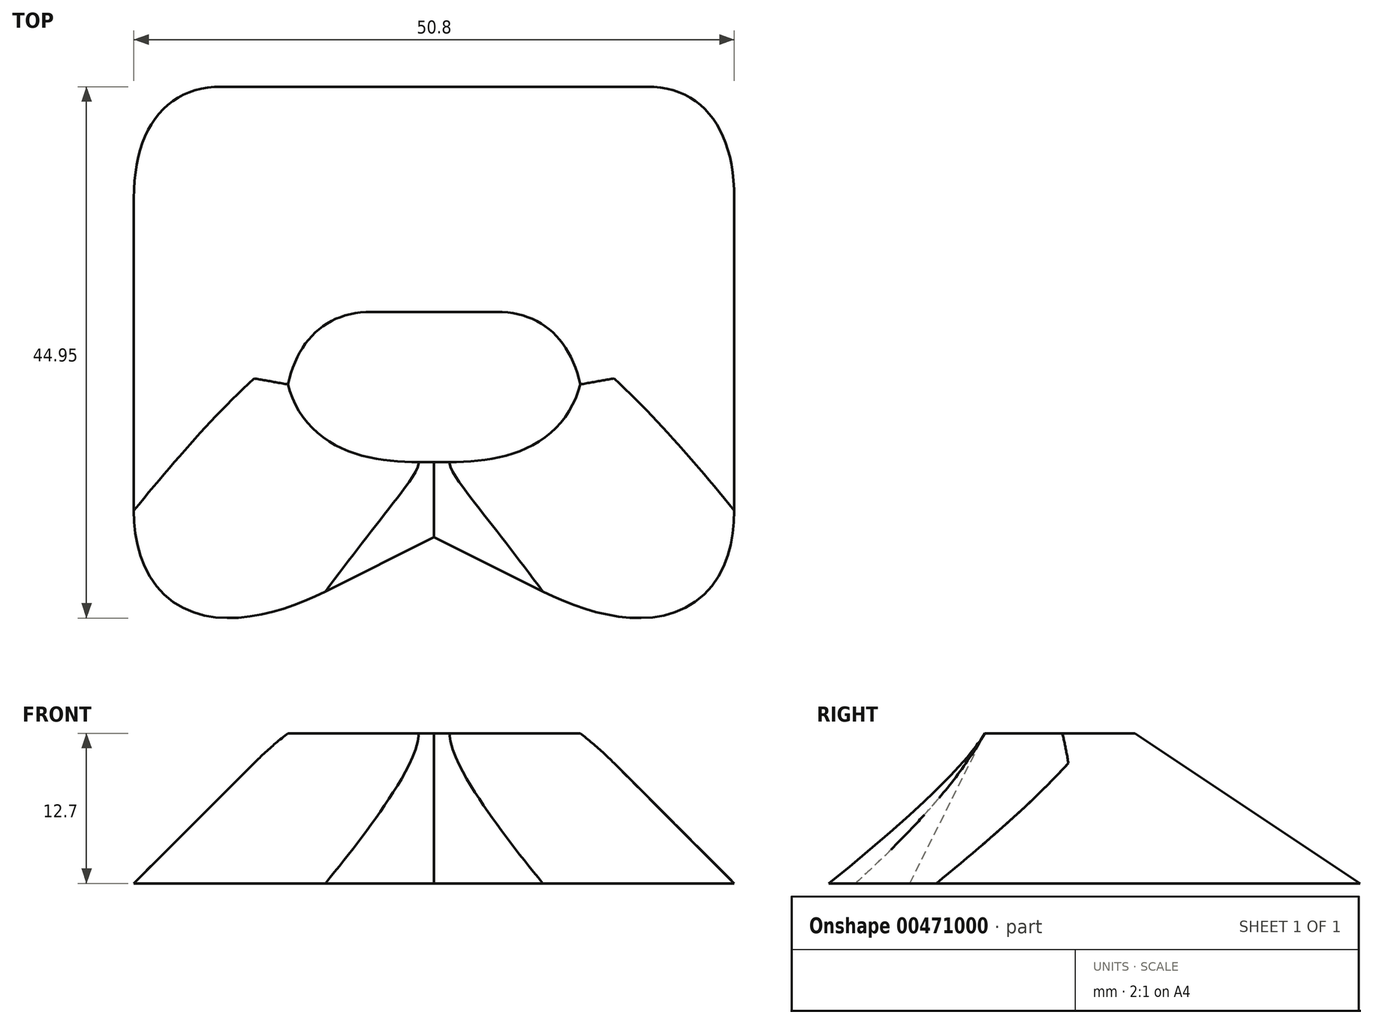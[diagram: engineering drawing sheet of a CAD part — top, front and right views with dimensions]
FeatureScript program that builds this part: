
annotation { "Feature Type Name" : "Feature", "Feature Type Description" : "" }
export const myFeature = defineFeature(function(context is Context, id is Id, definition is map)
    precondition{}
    {
        {
            var Q0;
            Q0=qCreatedBy(makeId("Top.planeOp"),FACE);
            var sketch = newSketch(context, id + "F0", { "sketchPlane" : qUnion([Q0])});
            skLineSegment(sketch, "E0", {"start": v(25.4, 25.4) * mm, "end": v(-25.4, 25.4) * mm});
            skLineSegment(sketch, "E1", {"start": v(-25.4, 25.4) * mm, "end": v(-25.4, -25.4) * mm});
            skLineSegment(sketch, "E2", {"start": v(-25.4, -25.4) * mm, "end": v(0, -12.7) * mm});
            skLineSegment(sketch, "E3", {"start": v(0, -12.7) * mm, "end": v(25.4, -25.4) * mm});
            skLineSegment(sketch, "E4", {"start": v(25.4, -25.4) * mm, "end": v(25.4, 25.4) * mm});
            skPoint(sketch, "E5", {"position": v(25.4, 0) * mm});
            skPoint(sketch, "E6", {"position": v(-25.4, 0) * mm});
            skSolve(sketch);
        }
        {
            var Q0;
            Q0=qCreatedBy(makeId("Top.planeOp"),FACE);
            cPlane(context, id + "F1", {"entities" : qUnion([Q0]), "cplaneType" : CPlaneType.OFFSET, "offset" : 12.7 * mm, "width" : 152.4 * mm, "height" : 152.4 * mm});
        }
        {
            var Q0;
            Q0=qCreatedBy(id+"F1.planeOp",FACE);
            var sketch = newSketch(context, id + "F2", { "sketchPlane" : qUnion([Q0])});
            skLineSegment(sketch, "E7.bottom", {"start": v(12.7, 6.35) * mm, "end": v(-12.7, 6.35) * mm});
            skLineSegment(sketch, "E7.top", {"start": v(12.7, -6.35) * mm, "end": v(-12.7, -6.35) * mm});
            skLineSegment(sketch, "E7.left", {"start": v(12.7, 6.35) * mm, "end": v(12.7, -6.35) * mm});
            skLineSegment(sketch, "E7.right", {"start": v(-12.7, 6.35) * mm, "end": v(-12.7, -6.35) * mm});
            skPoint(sketch, "E7.middle", {"position": v(0, 0) * mm});
            skSolve(sketch);
        }
        {
            var Q0;
            Q0 = qSketchRegion(id + "F0", true);
            var Q1;
            Q1 = qSketchRegion(id + "F2", true);
            var Q2;
            Q2=sQuery(id+"F0.wireOp",VERTEX,"E2.start");
            var Q3;
            Q3=sQuery(id+"F2.wireOp",VERTEX,"E7.top.end");
            loft(context, id + "F3", {"sheetProfilesArray" : [{ "sheetProfileEntities" : qUnion([Q0]) }, { "sheetProfileEntities" : qUnion([Q1]) }], "matchConnections" : true, "connections" : [{ "connectionEntities" : qUnion([Q2, Q3]), "connectionEdgeQueries" : qUnion([]), "connectionEdgeParameters" : [] }]});
        }
        {
            var Q0;
            Q0=makeQuery(id+"F3.opLoft","SWEPT_EDGE",EDGE,{"disambiguationData":[OSD([sQuery(id+"F0.wireOp",EDGE,"E0"),sQuery(id+"F0.wireOp",EDGE,"E4"),sQuery(id+"F2.wireOp",EDGE,"E7.bottom"),sQuery(id+"F2.wireOp",EDGE,"E7.left")])]});
            var Q1;
            Q1=makeQuery(id+"F3.opLoft","SWEPT_EDGE",EDGE,{"disambiguationData":[OSD([sQuery(id+"F0.wireOp",EDGE,"E3"),sQuery(id+"F0.wireOp",EDGE,"E4"),sQuery(id+"F2.wireOp",EDGE,"E7.top"),sQuery(id+"F2.wireOp",EDGE,"E7.left")])]});
            var Q2;
            Q2=makeQuery(id+"F3.opLoft","SWEPT_EDGE",EDGE,{"disambiguationData":[OSD([sQuery(id+"F0.wireOp",EDGE,"E1"),sQuery(id+"F0.wireOp",EDGE,"E2"),sQuery(id+"F2.wireOp",EDGE,"E7.top"),sQuery(id+"F2.wireOp",EDGE,"E7.right")])]});
            var Q3;
            Q3=makeQuery(id+"F3.opLoft","SWEPT_EDGE",EDGE,{"disambiguationData":[OSD([sQuery(id+"F0.wireOp",EDGE,"E0"),sQuery(id+"F0.wireOp",EDGE,"E1"),sQuery(id+"F2.wireOp",EDGE,"E7.bottom"),sQuery(id+"F2.wireOp",EDGE,"E7.right")])]});
            fillet(context, id + "F4", {"entities" : qUnion([Q0, Q1, Q2, Q3]), "radius" : 12.7 * mm, "tangentPropagation" : true, "allowEdgeOverflow" : false});
        }
    });
